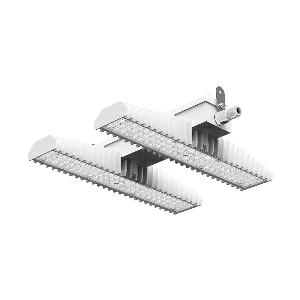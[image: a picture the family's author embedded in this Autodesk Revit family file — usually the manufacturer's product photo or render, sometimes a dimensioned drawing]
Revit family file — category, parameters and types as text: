
# Revit family: 3f_filippi_-_3f_lem_ho_concentrato_3f_filippi_-_58978_-_3f_lem_2_ho_led_140_dali_cr_conc
name_source: partatom
category: Lighting Fixtures
units: mm (PartAtom-declared; Revit-internal decimal feet)

## family parameters
Cut with Voids When Loaded = No
Host = Face
Light Source = No
Part Type = Normal
Room Calculation Point = No
Round Connector Dimension = Use Diameter
Shared = No

## types (1)
- 3F Filippi - 3F LEM HO Concentrato (1 x LED, 21649 lm, 138 W, 4000 K)
    Apparent Load = 138 VA
    Approval mark = CE
    CIE Flux Codes = 83 96 99 100 100
    Color Rendering = 80
    Color Temperature = 4000 K
    Control Gear = Electronic transformer
    Default Elevation = 1800 mm
    Description = Industrial luminaire with high light output and high luminous efficiency designed with the most innovative technologies for environments with temperature up to 55°C.

ILLUMINOTECHNICAL
Luminous efficiency 100% (DLOR 100%, ULOR 0%).
Initial luminous flux of the luminaire 21649 lm.
Direct symmetric narrow distribution: the illuminated area has a elliptical shape.
Installation Interdistance Transv.D = 0.52 x hu - Long.D = 1.16 x hu.
Tabular UGR (CIE 117 - 4H-8H; S=0.25H; 70/50/20): RUG 17.8 - 21.6.
Beam angle: 31° - 73°.
Luminous efficacy 157 lm/W.
Lifetime (L93/B10): 30000 h. (tq+25°C)
Lifetime (L90/B10): 50000 h. (tq+25°C)
Lifetime (L85/B10): 80000 h. (tq+25°C)
Lifetime (L80/B10): 100000 h. (tq+25°C)
Lifetime (L85/B10): 50000 h. (tq+55°C)
Sudden decreased luminous flux after 50000 hours: 0% (C0).
Photobiological safety in compliance with IEC/TR 62778: RG0 risk exempt, (IEC 62471).
In compliance with IEC/EN 62722-2-1 - IEC/EN 62717 standards.

SOURCE
2 Mid-Power linear LED modules 70W/840.
Energy efficiency class (UE 2019/2020 - UE 2019/2015): C.
CIE 13.3 Colour rendering index: CRI >80 (R9 <50%).
IES TM-30 Fidelity Index: Rf = 84 Rg = 95.
CCT nominal colour temperature 4000 K.
Colour initial tolerance (MacAdam): SDCM 3.

MECHANICAL
Passive modular heatsinks in die-casted aluminium, painted in white colour.
To optimize the thermal management of the LED module, the heatsinks are oversized and provided with self-cleaning of cooling fins.
Wiring body in aluminium and galvanised steel anchored solidly to the sinks and thermally separated.
3F Lens lenses with high luminous efficiency, transparent methacrylate (PMMA), fixed to the LED modules.
Fixing brackets in stainless steel.
Luminaire with limited surface temperature. - D - (EN 60598-2-24)
Dimensions: 470x542 mm, height 129 mm. Weight 9.46 kg.
IP65 protection degree.
Mechanical strength to impacts IK06 (1 joule).
Glow-wire test resistance 650°C.

ELECTRICAL
Halogen Free DALI-2 DATI (Parts 251, 252, 253), PUSH-DIM, electronic wiring 230V-50/60Hz, power factor 0.97 at full load, THD <25%, constant output current, class I, 1 driver, 1 DALI addresse.
Power of the luminaire 138 W.
ENEC - CE.
SAFE FLICKER: PstLM=<1 and SVM=<0.4 (IEC TR 61547-1 and IEC TR 63158), to ensure a more comfortable and safe light.
Luminaire compliant with EN 60598-2-22 for power supply from a centralised emergency system CPSS (Central Power Supply System), not incorporated in the luminaire - high risk areas excluded. The default power and flux are 100% in AC and 15% in DC.
Ambient temperature from -30°C to +55°C.
Temperature class T6 max 85°C.
Quick connection via M25 5P connector with 9-13 mm tightening range.
Power unit positioned on a separate compartment by the LED module to ensure optimum temperatures of cabling components, to be inspectable and maintainable.
Relative humidity UR: <85%.

INSTALLATION
Ceiling / Suspended / Wall.
All accessories dedicated to this product are available on the Catalog and on our website www.3F-Filippi.com.

APPLICATIONS
In commercial environments, exhibition and industrial areas, stores, open areas or with shelves.
Environments in which it is necessary a total protection against falling fragments (eg environments with foodstuffs or machines with moving parts or with extreme temperature changes), use luminaires with polycarbonate lenses.

LIGHT MANAGEMENT
Recommended minimum setting: 10%.
The luminaire, equipped with (DALI-2 DATI) driver, can be controlled manually with 3F Easy Dim technology or automatically/manually with wired or wireless DALI/D2D control systems.
The D2D driver guarantees interoperability with other devices with the same certification by making the following information available:
Device Data (Part 251), Energy Report (Part 252), Diagnosis & Maintenance (Part 253).
In electrical systems without a regulation system (manual or automatic) and DALI bus, a suitable jumper must be made on the DA-DA terminals of the appliance.

WARNING
Fixture not suitable for cold stores with an ambient temperature <0°C and/or relative humidity >85%.
Luminaire designed for disposal/recycling at end-of-life.
Replaceable (LED only) light source by a professional. Replaceable control gear by a professional.
    Height = 129 mm
    Lamp = 1 x LED
    Lamp Light Flux = 21649 lm
    Lamp Power = 138 W
    Lamp count = 1
    Length = 470 mm
    Lifetime = 50000 h
    Luminous efficacy = 157 lm/W
    Manufacturer = 3F Filippi
    ModVariant = No
    Model = 3F Filippi - 58978 - 3F LEM 2 HO LED 140 DALI CR CONC
    Mounting Place = Ceiling
    Mounting Type = Pendant
    Number of Poles = 1
    OnlyDefault = Yes
    Power Factor = 1
    Product Name = 3F Filippi - 3F LEM HO Concentrato
    Product group = pendant luminaire
    ProductGroupID = 9
    Protection Class = Protection class I
    Protection Degree = IP 65
    RLX_Detail_Level = 1
    RLX_Emergency_Light_Flux = 0 lm
    RLX_Emergency_Type = 0
    RLX_Emergency_Type_DB = No
    RlxData = <blob elided: 98649 chars, md5=72ea5b39>
    Socket = socket
    Standby Power = 0 W
    System Light Flux = 21649 lm
    System Power = 138 W
    Type Comments = Product without accessories
    Type Image = 3f_filippi_-_lem_2.jpg
    URL = http://relux.com
    VarID = ---
    Voltage = 0 V
    Weight = 0.00 kg
    Width = 542 mm

## geometry (parser evidence)
native form markers: Blend x4, Sweep x11
no freeform markers — native parametric forms only
